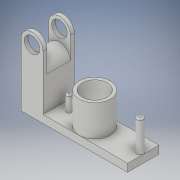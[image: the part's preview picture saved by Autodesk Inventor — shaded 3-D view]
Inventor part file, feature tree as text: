
AUTODESK INVENTOR PART (.ipt)
format: ipt  version: 2019 (Build 230136000, 136)  size: 184,320 bytes
history: native  units: in
note: dims shown in document units (in); Inventor stores cm internally (conversion verified against a paired STEP export)
features: sketch x6, extrude x5, fillet x3
ambient origin geometry x8: Origin, YZ Plane, XZ Plane, XY Plane, X Axis, Y Axis, Z Axis, Center Point
bodies: Solid1 (feature_tree)
feature tree (14):
  extrude  "Extrusion1"  Depth=0.1969in
  extrude  "Extrusion2"  Depth=0.3937in
  extrude  "Extrusion3"  Depth=2.126in
  fillet  "Fillet1"  Radius=0.7874in
  fillet  "Fillet2"  Radius=0.1181in
  extrude  "Extrusion4"  Depth=0.7874in
  sketch  "Sketch6"  dims[d16=0.9055in d19=0.3937in d20=0.1575in]
  extrude  "Extrusion5"  Depth=0.3937in
  fillet  "Fillet3"  Radius=0.1575in
  sketch  "Sketch1"  dims[d0=1.5748in d2=0.1969in]
  sketch  "Sketch2"  dims[d6=0.2756in d7=0.3937in]
  sketch  "Sketch4"  dims[d8=0.5512in d9=2.126in d10=0.7874in d11=0.0in d12=0.1181in]
  sketch  "Sketch5"  dims[d13=0.2559in d14=0.7874in]
  sketch  "Sketch7"  dims[d21=0.3937in d22=0.6693in d23=0.7874in d24=0.0in d25=0.3937in d26=0.7874in d27=0.0in d28=0.0394in d29=0.0394in d30=0.6299in d31=1.1811in d32=0.0in d40=0.5512in d41=0.5512in d42=0.5906in d43=0.5512in d44=0.0in d45=0.2756in]
